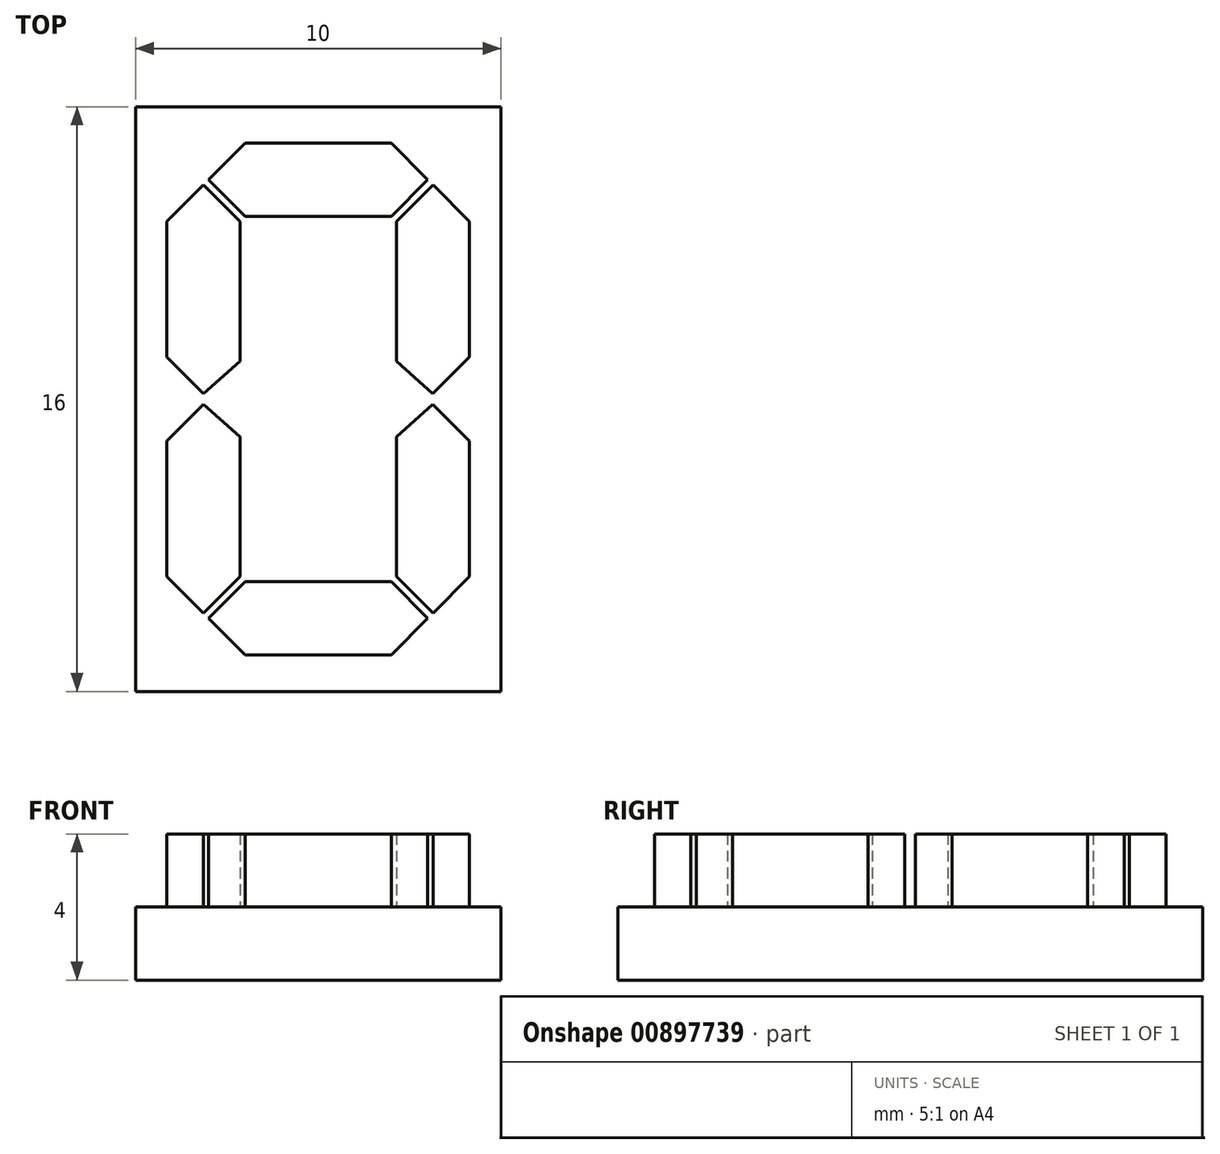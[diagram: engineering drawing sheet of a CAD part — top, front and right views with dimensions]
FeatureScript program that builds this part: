
annotation { "Feature Type Name" : "Feature", "Feature Type Description" : "" }
export const myFeature = defineFeature(function(context is Context, id is Id, definition is map)
    precondition{}
    {
        {
            var Q0;
            Q0=qCreatedBy(makeId("Top.planeOp"),FACE);
            var sketch = newSketch(context, id + "F0", { "sketchPlane" : qUnion([Q0])});
            skLineSegment(sketch, "E0.bottom", {"start": v(5, -8) * mm, "end": v(-5, -8) * mm});
            skLineSegment(sketch, "E0.top", {"start": v(5, 8) * mm, "end": v(-5, 8) * mm});
            skLineSegment(sketch, "E0.left", {"start": v(5, -8) * mm, "end": v(5, 8) * mm});
            skLineSegment(sketch, "E0.right", {"start": v(-5, -8) * mm, "end": v(-5, 8) * mm});
            skPoint(sketch, "E0.middle", {"position": v(0, 0) * mm});
            skSolve(sketch);
        }
        {
            var Q0;
            Q0=makeQuery(id+"F0.imprint","IMPRINT",FACE,{"disambiguationData":[TD([[makeQuery(id+"F0.imprint","IMPRINT",EDGE,{"derivedFrom":sQuery(id+"F0.wireOp",EDGE,"E0.bottom")}),-1.0]])]});
            extrude(context, id + "F1", {"entities" : qUnion([Q0]), "depth" : 2 * mm, "offsetDistance" : 25 * mm});
        }
        {
            var Q0;
            Q0=makeQuery(id+"F1.opExtrude","CAP_FACE",FACE,{"disambiguationData":[OSD([sQuery(id+"F0.wireOp",EDGE,"E0.bottom"),sQuery(id+"F0.wireOp",EDGE,"E0.top"),sQuery(id+"F0.wireOp",EDGE,"E0.left"),sQuery(id+"F0.wireOp",EDGE,"E0.right")])],"isStart":false});
            var sketch = newSketch(context, id + "F2", { "sketchPlane" : qUnion([Q0])});
            skLineSegment(sketch, "E1", {"start": v(-3, 8) * mm, "end": v(-3, -8) * mm, "construction": true});
            skLineSegment(sketch, "E2.0.1.0", {"start": v(-5, 6) * mm, "end": v(5, 6) * mm, "construction": true});
            skLineSegment(sketch, "E2.direction2", {"start": v(-5, 7) * mm, "end": v(-5, 6) * mm, "construction": true});
            skLineSegment(sketch, "E3.1.0.0", {"start": v(-2, 8) * mm, "end": v(-2, -8) * mm, "construction": true});
            skLineSegment(sketch, "E3.3.0.0", {"start": v(0, 8) * mm, "end": v(0, -8) * mm, "construction": true});
            skLineSegment(sketch, "E3.direction1", {"start": v(-3, -8) * mm, "end": v(-2, -8) * mm, "construction": true});
            skLineSegment(sketch, "E4", {"start": v(-2, 7) * mm, "end": v(-3, 6) * mm});
            skLineSegment(sketch, "E5", {"start": v(-3, 6) * mm, "end": v(-2, 5) * mm});
            skLineSegment(sketch, "E6", {"start": v(-2, 5) * mm, "end": v(0, 5) * mm});
            skLineSegment(sketch, "E7", {"start": v(-2, 7) * mm, "end": v(0, 7) * mm});
            skLineSegment(sketch, "E8.0", {"start": v(-3.14, 5.86) * mm, "end": v(-2.14, 4.86) * mm});
            skLineSegment(sketch, "E9", {"start": v(-2.14, 4.86) * mm, "end": v(-2.14, 1.03) * mm});
            skLineSegment(sketch, "E10.0", {"start": v(-4.14, 4.86) * mm, "end": v(-4.14, 1.15) * mm});
            skLineSegment(sketch, "E11", {"start": v(-3.14, 5.86) * mm, "end": v(-4.14, 4.86) * mm});
            skLineSegment(sketch, "E12", {"start": v(-4.14, 4.86) * mm, "end": v(5, 4.86) * mm, "construction": true});
            skLineSegment(sketch, "E13", {"start": v(0, 0.9) * mm, "end": v(-2, 0.9) * mm, "construction": true});
            skLineSegment(sketch, "E14", {"start": v(-2, 0.9) * mm, "end": v(-3, 0) * mm, "construction": true});
            skLineSegment(sketch, "E15.0", {"start": v(-2.14, 1.03) * mm, "end": v(-3.14, 0.15) * mm});
            skLineSegment(sketch, "E16", {"start": v(-3.14, 5.86) * mm, "end": v(-3.14, 0.15) * mm, "construction": true});
            skLineSegment(sketch, "E17", {"start": v(-4.14, 1.15) * mm, "end": v(-3.14, 0.15) * mm});
            skLineSegment(sketch, "E18.MirrorCS", {"start": v(0, -0.9) * mm, "end": v(-2, -0.9) * mm, "construction": true});
            skLineSegment(sketch, "E19.MirrorCS", {"start": v(-2, -0.9) * mm, "end": v(-3, 0) * mm, "construction": true});
            skLineSegment(sketch, "E20.MirrorCS", {"start": v(-2, -5) * mm, "end": v(0, -5) * mm});
            skLineSegment(sketch, "E21.MirrorCS", {"start": v(-3, -6) * mm, "end": v(-2, -5) * mm});
            skLineSegment(sketch, "E22.MirrorCS", {"start": v(-2, -7) * mm, "end": v(-3, -6) * mm});
            skLineSegment(sketch, "E23.MirrorCS", {"start": v(-2, -7) * mm, "end": v(0, -7) * mm});
            skLineSegment(sketch, "E24.MirrorCS", {"start": v(-3.14, -5.86) * mm, "end": v(-2.14, -4.86) * mm});
            skLineSegment(sketch, "E25.MirrorCS", {"start": v(-3.14, -5.86) * mm, "end": v(-4.14, -4.86) * mm});
            skLineSegment(sketch, "E26.MirrorCS", {"start": v(-4.14, -4.86) * mm, "end": v(-4.14, -1.15) * mm});
            skLineSegment(sketch, "E27.MirrorCS", {"start": v(-4.14, -1.15) * mm, "end": v(-3.14, -0.15) * mm});
            skLineSegment(sketch, "E28.MirrorCS", {"start": v(-2.14, -4.86) * mm, "end": v(-2.14, -1.03) * mm});
            skLineSegment(sketch, "E29.MirrorCS", {"start": v(-2.14, -1.03) * mm, "end": v(-3.14, -0.15) * mm});
            skLineSegment(sketch, "E30.MirrorCS", {"start": v(2, 7) * mm, "end": v(0, 7) * mm});
            skLineSegment(sketch, "E31.MirrorCS", {"start": v(2, 7) * mm, "end": v(3, 6) * mm});
            skLineSegment(sketch, "E32.MirrorCS", {"start": v(3, 6) * mm, "end": v(2, 5) * mm});
            skLineSegment(sketch, "E33.MirrorCS", {"start": v(2, 5) * mm, "end": v(0, 5) * mm});
            skLineSegment(sketch, "E34.MirrorCS", {"start": v(3.14, 5.86) * mm, "end": v(2.14, 4.86) * mm});
            skLineSegment(sketch, "E35.MirrorCS", {"start": v(3.14, 5.86) * mm, "end": v(4.14, 4.86) * mm});
            skLineSegment(sketch, "E36.MirrorCS", {"start": v(4.14, 4.86) * mm, "end": v(4.14, 1.15) * mm});
            skLineSegment(sketch, "E37.MirrorCS", {"start": v(4.14, 1.15) * mm, "end": v(3.14, 0.15) * mm});
            skLineSegment(sketch, "E38.MirrorCS", {"start": v(2.14, 4.86) * mm, "end": v(2.14, 1.03) * mm});
            skLineSegment(sketch, "E39.MirrorCS", {"start": v(2.14, 1.03) * mm, "end": v(3.14, 0.15) * mm});
            skLineSegment(sketch, "E40.MirrorCS", {"start": v(2, 0.9) * mm, "end": v(3, 0) * mm, "construction": true});
            skLineSegment(sketch, "E41.MirrorCS", {"start": v(0, 0.9) * mm, "end": v(2, 0.9) * mm, "construction": true});
            skLineSegment(sketch, "E42.MirrorCS", {"start": v(2, -0.9) * mm, "end": v(3, 0) * mm, "construction": true});
            skLineSegment(sketch, "E43.MirrorCS", {"start": v(0, -0.9) * mm, "end": v(2, -0.9) * mm, "construction": true});
            skLineSegment(sketch, "E44.MirrorCS", {"start": v(2.14, -1.03) * mm, "end": v(3.14, -0.15) * mm});
            skLineSegment(sketch, "E45.MirrorCS", {"start": v(4.14, -1.15) * mm, "end": v(3.14, -0.15) * mm});
            skLineSegment(sketch, "E46.MirrorCS", {"start": v(4.14, -4.86) * mm, "end": v(4.14, -1.15) * mm});
            skLineSegment(sketch, "E47.MirrorCS", {"start": v(2.14, -4.86) * mm, "end": v(2.14, -1.03) * mm});
            skLineSegment(sketch, "E48.MirrorCS", {"start": v(3.14, -5.86) * mm, "end": v(2.14, -4.86) * mm});
            skLineSegment(sketch, "E49.MirrorCS", {"start": v(3.14, -5.86) * mm, "end": v(4.14, -4.86) * mm});
            skLineSegment(sketch, "E50.MirrorCS", {"start": v(3, -6) * mm, "end": v(2, -5) * mm});
            skLineSegment(sketch, "E51.MirrorCS", {"start": v(2, -5) * mm, "end": v(0, -5) * mm});
            skLineSegment(sketch, "E52.MirrorCS", {"start": v(2, -7) * mm, "end": v(3, -6) * mm});
            skLineSegment(sketch, "E53.MirrorCS", {"start": v(2, -7) * mm, "end": v(0, -7) * mm});
            skSolve(sketch);
        }
        {
            var Q0;
            Q0=qSketchRegion(id+"F2",true);
            extrude(context, id + "F3", {"entities" : qUnion([Q0]), "operationType" : NewBodyOperationType.ADD, "depth" : 2 * mm, "offsetDistance" : 25 * mm});
        }
    });
